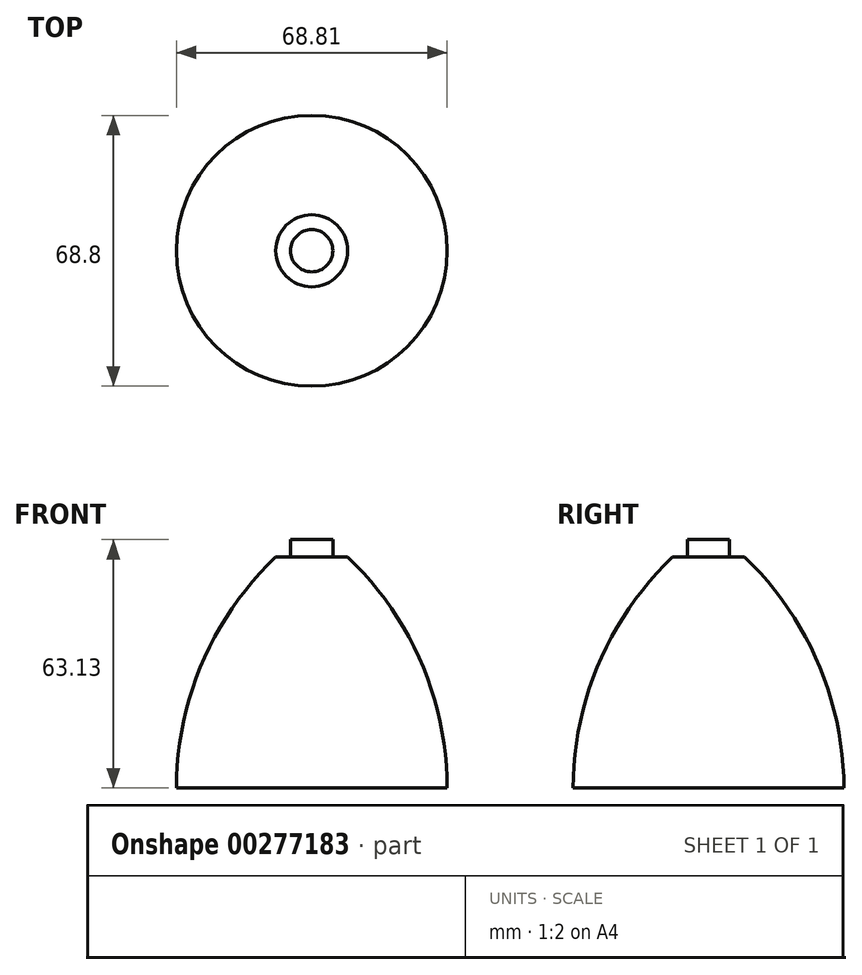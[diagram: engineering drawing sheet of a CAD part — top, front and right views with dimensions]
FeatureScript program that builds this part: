
annotation { "Feature Type Name" : "Feature", "Feature Type Description" : "" }
export const myFeature = defineFeature(function(context is Context, id is Id, definition is map)
    precondition{}
    {
        {
            var Q0;
            Q0=qCreatedBy(makeId("Front.planeOp"),FACE);
            var sketch = newSketch(context, id + "F0", { "sketchPlane" : qUnion([Q0])});
            skArc(sketch, "E0", {"start": v(-3.79, 68.66) * mm, "mid": v(-22.41, 41.89) * mm, "end": v(-29.04, 9.95) * mm});
            skLineSegment(sketch, "E1", {"start": v(-3.79, 68.66) * mm, "end": v(0, 68.66) * mm});
            skLineSegment(sketch, "E2", {"start": v(0, 68.66) * mm, "end": v(0, 73.08) * mm});
            skLineSegment(sketch, "E3", {"start": v(0, 73.08) * mm, "end": v(5.37, 73.08) * mm});
            skLineSegment(sketch, "E4", {"start": v(5.37, 9.95) * mm, "end": v(5.37, 73.08) * mm});
            skLineSegment(sketch, "E5", {"start": v(5.37, 9.95) * mm, "end": v(-29.04, 9.95) * mm});
            skSolve(sketch);
        }
        {
            var Q0;
            Q0=makeQuery(id+"F0.imprint","IMPRINT",FACE,{"disambiguationData":[TD([[makeQuery(id+"F0.imprint","IMPRINT",EDGE,{"derivedFrom":sQuery(id+"F0.wireOp",EDGE,"E0")}),1.0]])]});
            var Q1;
            Q1=sQuery(id+"F0.wireOp",EDGE,"E4");
            revolve(context, id + "F1", {"entities" : qUnion([Q0]), "axis" : qUnion([Q1]), "revolveType" : RevolveType.FULL});
        }
    });
